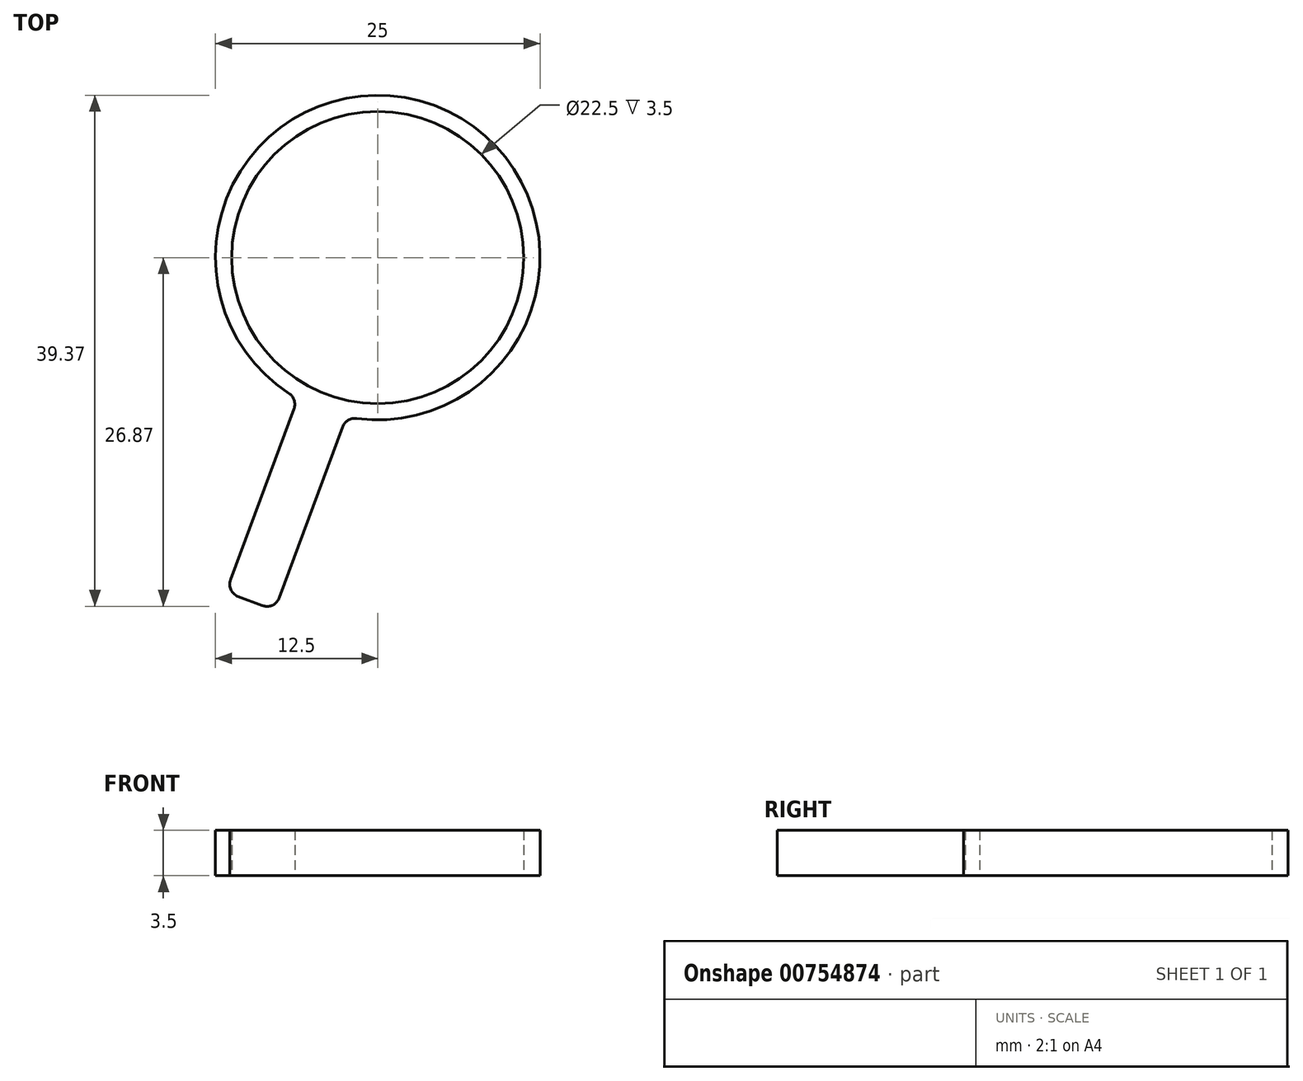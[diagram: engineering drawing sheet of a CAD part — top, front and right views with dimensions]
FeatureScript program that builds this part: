
annotation { "Feature Type Name" : "Feature", "Feature Type Description" : "" }
export const myFeature = defineFeature(function(context is Context, id is Id, definition is map)
    precondition{}
    {
        {
            var Q0;
            Q0=qCreatedBy(makeId("Top.planeOp"),FACE);
            var sketch = newSketch(context, id + "F0", { "sketchPlane" : qUnion([Q0])});
            skCircle(sketch, "E0", {"center": v(0, 0) * mm, "radius": 12.5 * mm});
            skLineSegment(sketch, "E1", {"start": v(-6.17, -10.87) * mm, "end": v(-11.69, -25.76) * mm});
            skLineSegment(sketch, "E2", {"start": v(-11.69, -25.76) * mm, "end": v(-7.94, -27.16) * mm});
            skLineSegment(sketch, "E3", {"start": v(-7.94, -27.16) * mm, "end": v(-2.42, -12.26) * mm});
            skPoint(sketch, "E4", {"position": v(-9.81, -26.46) * mm});
            skLineSegment(sketch, "E5", {"start": v(0, 0) * mm, "end": v(-9.81, -26.46) * mm, "construction": true});
            skSolve(sketch);
        }
        {
            var Q0;
            Q0 = qSketchRegion(id + "F0", true);
            extrude(context, id + "F1", {"entities" : qUnion([Q0]), "depth" : 3.5 * mm, "offsetDistance" : 25 * mm});
        }
        {
            var Q0;
            Q0=makeQuery(id+"F1.opExtrude","CAP_FACE",FACE,{"disambiguationData":[OSD([sQuery(id+"F0.wireOp",EDGE,"E0"),sQuery(id+"F0.wireOp",EDGE,"E1"),sQuery(id+"F0.wireOp",EDGE,"E2"),sQuery(id+"F0.wireOp",EDGE,"E3")])],"isStart":true});
            var sketch = newSketch(context, id + "F2", { "sketchPlane" : qUnion([Q0])});
            skCircle(sketch, "E6", {"center": v(0, 0) * mm, "radius": 11.25 * mm});
            skSolve(sketch);
        }
        {
            var Q0;
            Q0 = qSketchRegion(id + "F2", true);
            extrude(context, id + "F3", {"entities" : qUnion([Q0]), "operationType" : NewBodyOperationType.REMOVE, "endBound" : BoundingType.THROUGH_ALL, "oppositeDirection" : true, "depth" : 25 * mm, "offsetDistance" : 25 * mm});
        }
        {
            var Q0;
            Q0=makeQuery(id+"F1.opExtrude","SWEPT_EDGE",EDGE,{"disambiguationData":[OSD([sQuery(id+"F0.wireOp",EDGE,"E2"),sQuery(id+"F0.wireOp",EDGE,"E3")])]});
            var Q1;
            Q1=makeQuery(id+"F1.opExtrude","SWEPT_EDGE",EDGE,{"disambiguationData":[OSD([sQuery(id+"F0.wireOp",EDGE,"E1"),sQuery(id+"F0.wireOp",EDGE,"E2")])]});
            var Q2;
            Q2=makeQuery(id+"F1.opExtrude","SWEPT_EDGE",EDGE,{"disambiguationData":[OSD([sQuery(id+"F0.wireOp",EDGE,"E0"),sQuery(id+"F0.wireOp",EDGE,"E3")])]});
            var Q3;
            Q3=makeQuery(id+"F1.opExtrude","SWEPT_EDGE",EDGE,{"disambiguationData":[OSD([sQuery(id+"F0.wireOp",EDGE,"E0"),sQuery(id+"F0.wireOp",EDGE,"E1")])]});
            fillet(context, id + "F4", {"entities" : qUnion([Q0, Q1, Q2, Q3]), "radius" : 1 * mm, "tangentPropagation" : true, "allowEdgeOverflow" : false});
        }
    });
